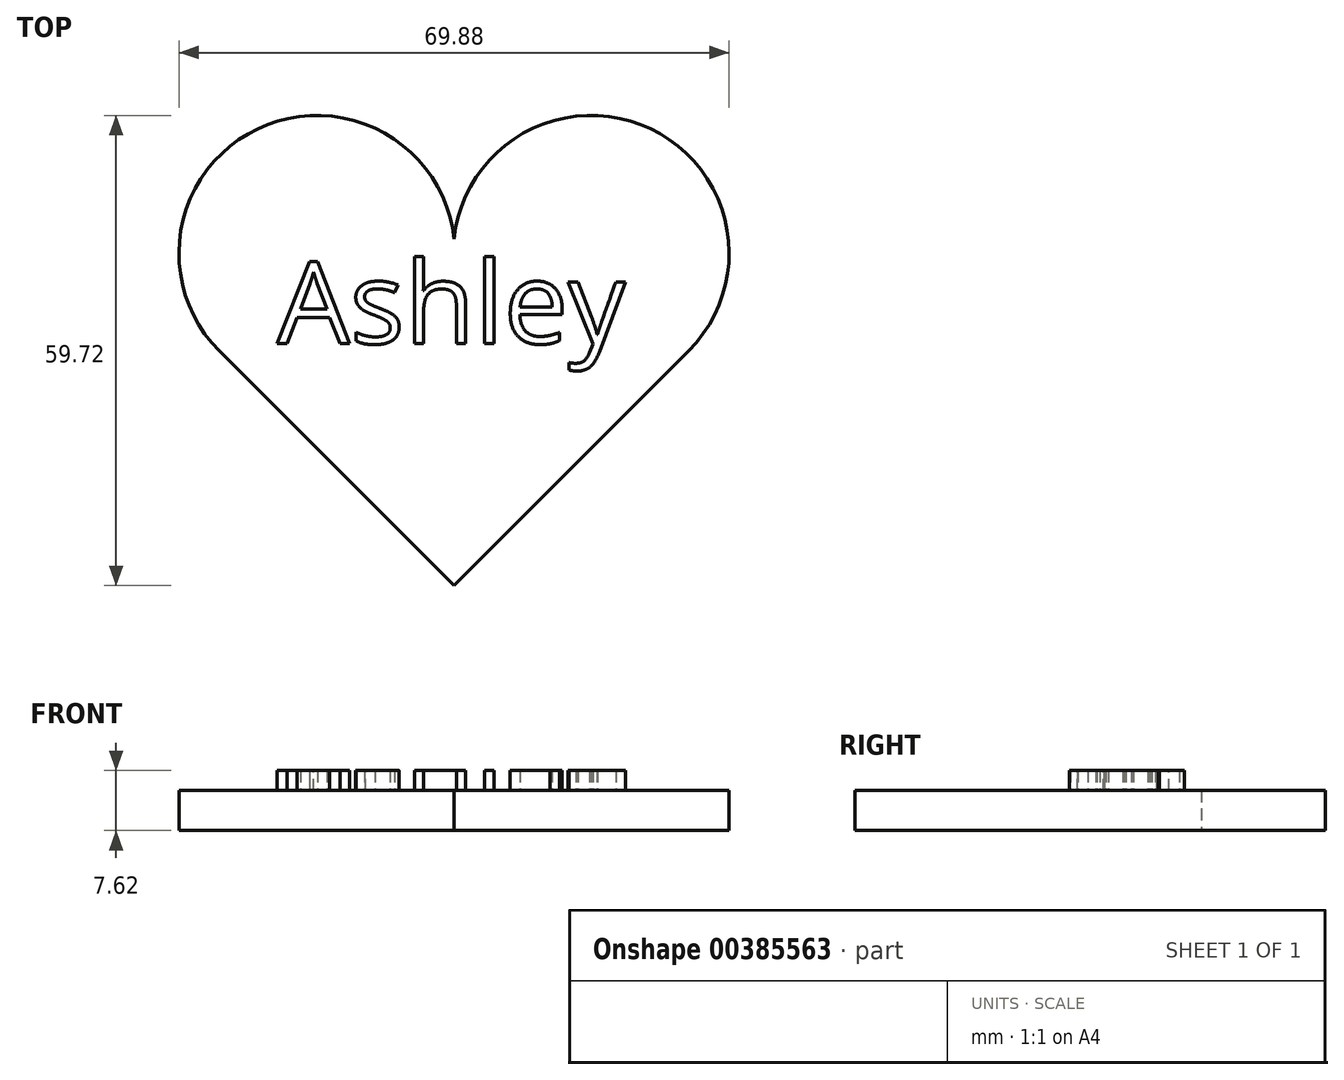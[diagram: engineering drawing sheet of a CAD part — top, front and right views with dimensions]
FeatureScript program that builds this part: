
annotation { "Feature Type Name" : "Feature", "Feature Type Description" : "" }
export const myFeature = defineFeature(function(context is Context, id is Id, definition is map)
    precondition{}
    {
        {
            var Q0;
            Q0=qCreatedBy(makeId("Top.planeOp"),FACE);
            var sketch = newSketch(context, id + "F0", { "sketchPlane" : qUnion([Q0])});
            skLineSegment(sketch, "E0", {"start": v(0, 0) * mm, "end": v(29.8, 29.82) * mm});
            skLineSegment(sketch, "E1", {"start": v(0, 0) * mm, "end": v(-29.81, 29.8) * mm});
            skArc(sketch, "E2", {"start": v(-29.81, 29.8) * mm, "mid": v(-24.97, 58) * mm, "end": v(0, 44.02) * mm});
            skArc(sketch, "E3", {"start": v(29.8, 29.82) * mm, "mid": v(24.96, 58.02) * mm, "end": v(0, 44.02) * mm});
            skSolve(sketch);
        }
        {
            var Q0;
            Q0 = qSketchRegion(id + "F0", true);
            extrude(context, id + "F1", {"entities" : qUnion([Q0]), "depth" : 5.08 * mm});
        }
        {
            var Q0;
            Q0=qCreatedBy(makeId("Top.planeOp"),FACE);
            var sketch = newSketch(context, id + "F2", { "sketchPlane" : qUnion([Q0])});
            skText(sketch, "E4", { "text": "Ashley", "fontName": "OpenSans-Regular.ttf"});
            const initialGuessF2  = {"E4": [-0.02245, 0.03074, 1, 0, 0.01048]};
            skSetInitialGuess(sketch, initialGuessF2);
            skSolve(sketch);
        }
        {
            var Q0;
            Q0 = qSketchRegion(id + "F2", true);
            extrude(context, id + "F3", {"entities" : qUnion([Q0]), "operationType" : NewBodyOperationType.ADD, "depth" : 7.62 * mm});
        }
    });
